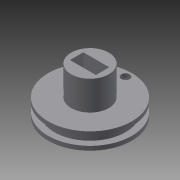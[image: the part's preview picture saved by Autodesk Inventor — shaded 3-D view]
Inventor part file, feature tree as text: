
AUTODESK INVENTOR PART (.ipt)
format: ipt  version: 2015 (Build 190159000, 159)  size: 116,224 bytes
history: native  units: mm
features: extrude x5, sketch x5
ambient origin geometry x8: Origin, YZ Plane, XZ Plane, XY Plane, X Axis, Y Axis, Z Axis, Center Point
bodies: Solid1 (feature_tree)
feature tree (10):
  extrude  "Extrusion1"  Depth=17.0mm
  extrude  "Extrusion2"  Depth=1.0mm
  extrude  "Extrusion3"  Depth=1.0mm TaperAngle=0.0deg
  extrude  "Extrusion4"  Depth=6.2mm
  extrude  "Extrusion5"  Depth=7.0mm
  sketch  "Sketch1"  dims[d0=20.0mm d1=17.0mm]
  sketch  "Sketch2"  dims[d2=1.0mm d3=0.0mm d4=17.0mm]
  sketch  "Sketch3"  dims[d5=2.0mm d6=0.0mm d7=1.0mm d8=0.0mm]
  sketch  "Sketch4"  dims[d9=9.0mm d10=6.2mm]
  sketch  "Sketch5"  dims[d11=3.2mm d12=1.51mm d13=3.1mm d14=7.0mm d15=0.0mm d16=2.0mm d17=7.0mm d18=0.0mm]
